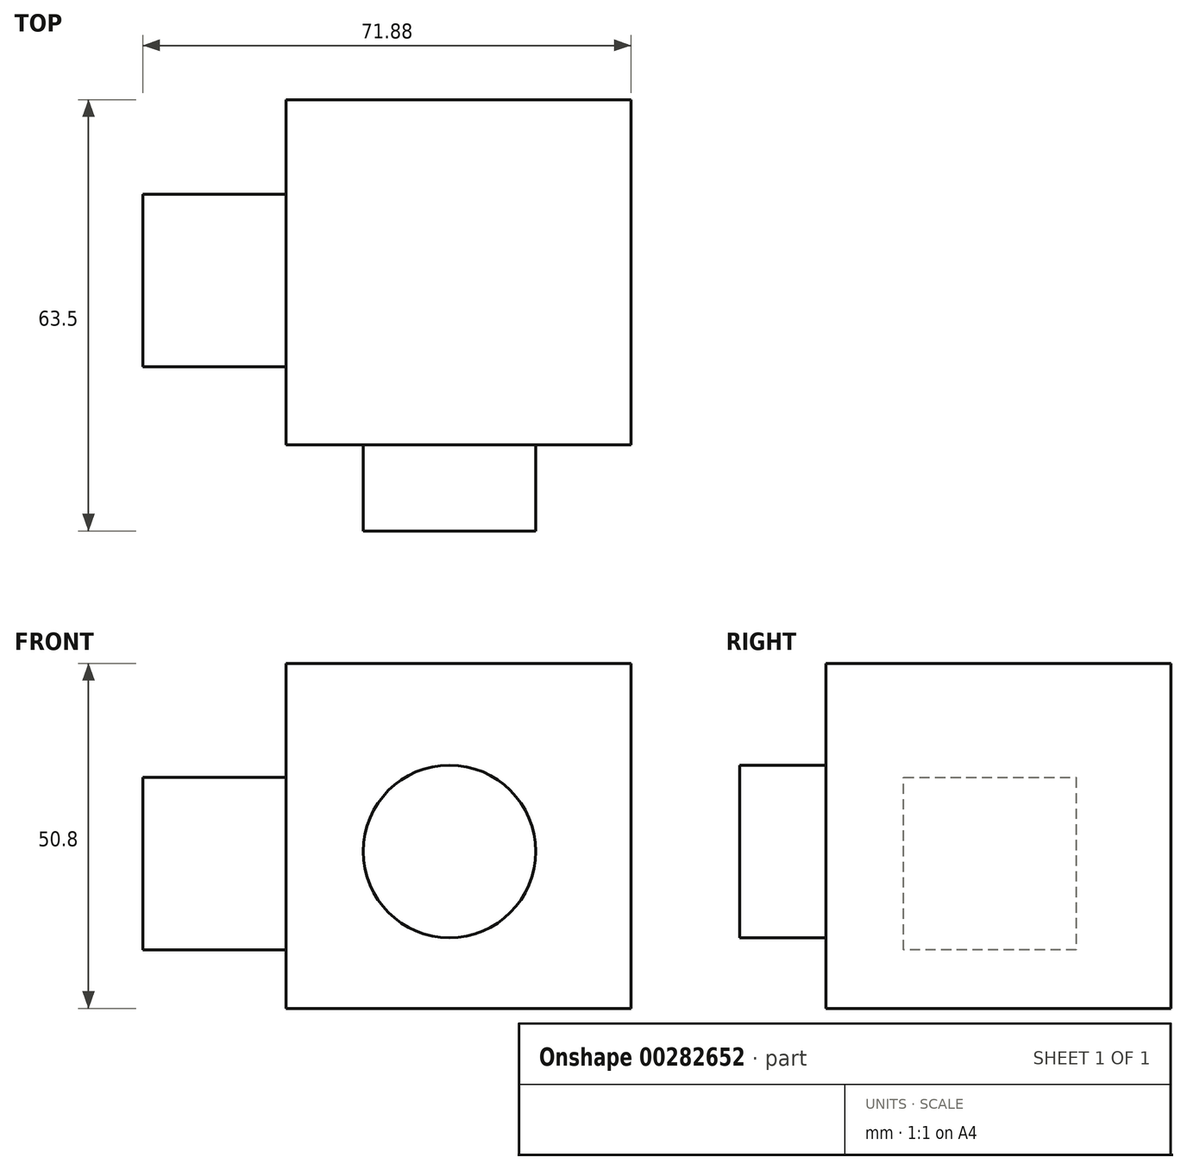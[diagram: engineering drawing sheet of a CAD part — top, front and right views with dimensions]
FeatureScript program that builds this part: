
annotation { "Feature Type Name" : "Feature", "Feature Type Description" : "" }
export const myFeature = defineFeature(function(context is Context, id is Id, definition is map)
    precondition{}
    {
        {
            var Q0;
            Q0=qCreatedBy(makeId("Front.planeOp"),FACE);
            var sketch = newSketch(context, id + "F0", { "sketchPlane" : qUnion([Q0])});
            skLineSegment(sketch, "E0.bottom", {"start": v(0, 0) * mm, "end": v(50.8, 0) * mm});
            skLineSegment(sketch, "E0.top", {"start": v(0, 50.8) * mm, "end": v(50.8, 50.8) * mm});
            skLineSegment(sketch, "E0.left", {"start": v(0, 0) * mm, "end": v(0, 50.8) * mm});
            skLineSegment(sketch, "E0.right", {"start": v(50.8, 0) * mm, "end": v(50.8, 50.8) * mm});
            skSolve(sketch);
        }
        {
            var Q0;
            Q0 = qSketchRegion(id + "F0", true);
            extrude(context, id + "F1", {"entities" : qUnion([Q0]), "depth" : 50.8 * mm});
        }
        {
            var Q0;
            Q0=qCreatedBy(makeId("Front.planeOp"),FACE);
            var sketch = newSketch(context, id + "F2", { "sketchPlane" : qUnion([Q0])});
            skCircle(sketch, "E1", {"center": v(24.06, 23.1) * mm, "radius": 12.7 * mm});
            skSolve(sketch);
        }
        {
            var Q0;
            Q0 = qSketchRegion(id + "F2", true);
            extrude(context, id + "F3", {"entities" : qUnion([Q0]), "operationType" : NewBodyOperationType.ADD, "depth" : 63.5 * mm});
        }
        {
            var Q0;
            Q0=qCreatedBy(makeId("Right.planeOp"),FACE);
            var sketch = newSketch(context, id + "F4", { "sketchPlane" : qUnion([Q0])});
            skLineSegment(sketch, "E2", {"start": v(-39.34, 33.99) * mm, "end": v(-13.94, 33.99) * mm});
            skLineSegment(sketch, "E3", {"start": v(-13.94, 33.99) * mm, "end": v(-13.94, 8.59) * mm});
            skLineSegment(sketch, "E4", {"start": v(-13.94, 8.59) * mm, "end": v(-39.34, 8.59) * mm});
            skLineSegment(sketch, "E5", {"start": v(-39.34, 8.59) * mm, "end": v(-39.34, 33.99) * mm});
            skSolve(sketch);
        }
        {
            var Q0;
            Q0 = qSketchRegion(id + "F4", true);
            extrude(context, id + "F5", {"entities" : qUnion([Q0]), "operationType" : NewBodyOperationType.ADD, "oppositeDirection" : true, "depth" : 21.08 * mm});
        }
    });
